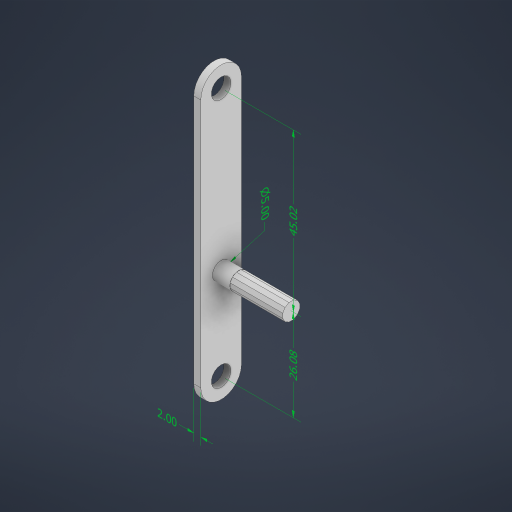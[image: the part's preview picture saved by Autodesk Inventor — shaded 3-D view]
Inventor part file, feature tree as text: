
AUTODESK INVENTOR PART (.ipt)
format: ipt  version: 2024 (Build 280153000, 153)  size: 503,296 bytes
history: native  units: mm
features: other x5, extrude x3, sketch x1
ambient origin geometry x8: Origin, YZ Plane, XZ Plane, XY Plane, X Axis, Y Axis, Z Axis, Center Point
bodies: Body1 (feature_tree)
feature tree (9):
  other  "솔리드1"
  sketch  "스케치1"
  extrude  "돌출1"  Depth=5.6mm
  extrude  "돌출2"  Depth=5.6mm
  extrude  "돌출3"  Depth=11.6mm
  other  "선형 치수 1"
  other  "선형 치수 2"
  other  "선형 치수 3"
  other  "지름 치수 1"
